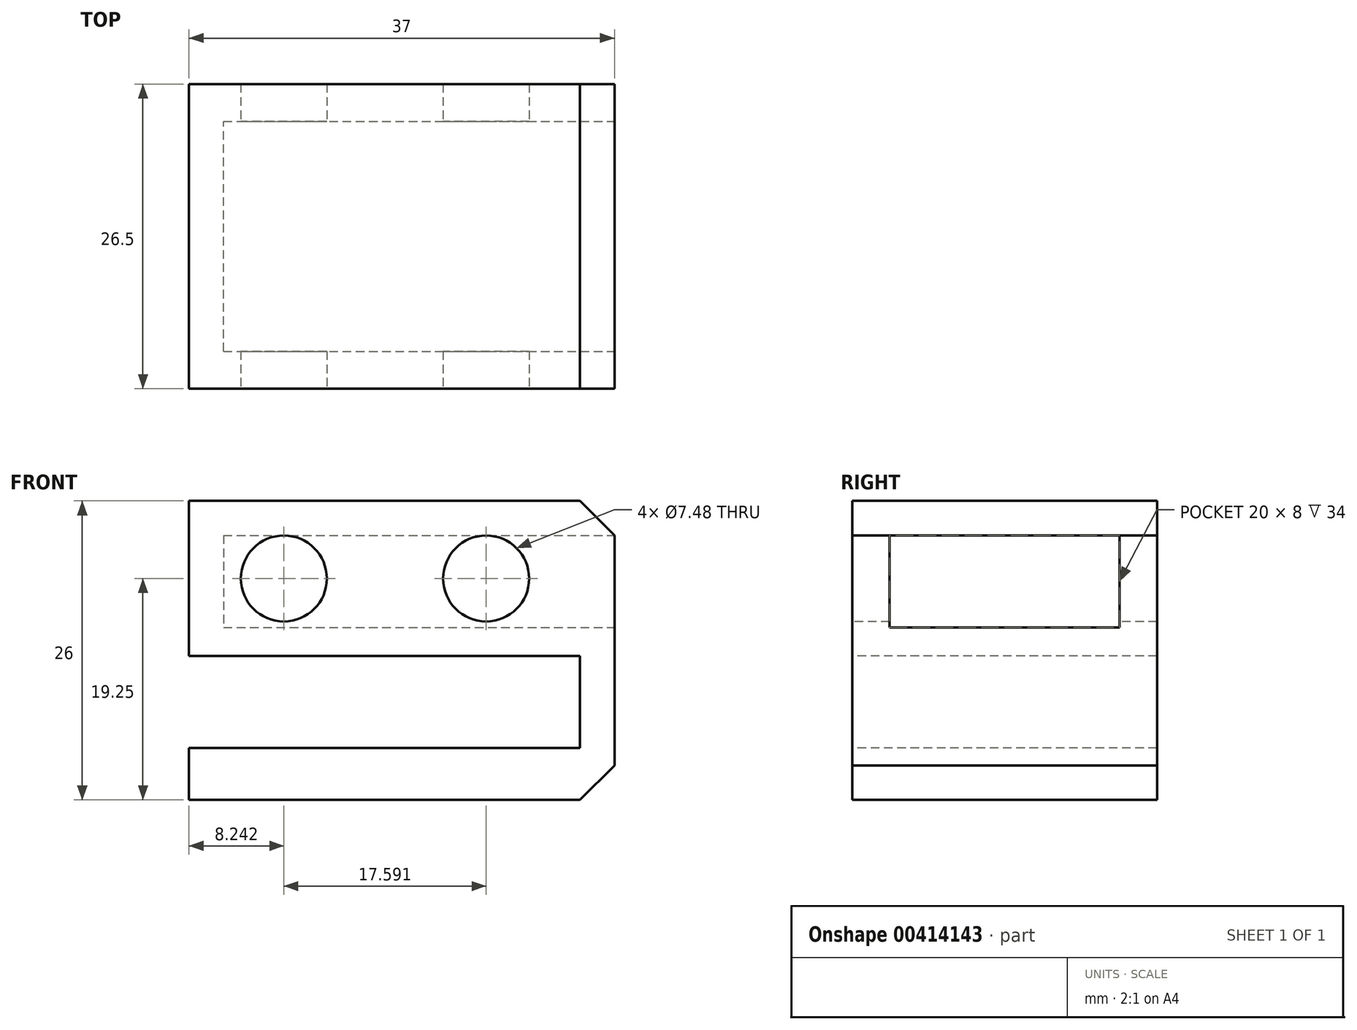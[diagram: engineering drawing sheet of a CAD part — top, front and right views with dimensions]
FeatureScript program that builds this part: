
annotation { "Feature Type Name" : "Feature", "Feature Type Description" : "" }
export const myFeature = defineFeature(function(context is Context, id is Id, definition is map)
    precondition{}
    {
        {
            var Q0;
            Q0=qCreatedBy(makeId("Top.planeOp"),FACE);
            var sketch = newSketch(context, id + "F0", { "sketchPlane" : qUnion([Q0])});
            skLineSegment(sketch, "E0.bottom", {"start": v(-28.8, 0) * mm, "end": v(8.2, 0) * mm});
            skLineSegment(sketch, "E0.top", {"start": v(-28.8, 26.5) * mm, "end": v(8.2, 26.5) * mm});
            skLineSegment(sketch, "E0.left", {"start": v(-28.8, 0) * mm, "end": v(-28.8, 26.5) * mm});
            skLineSegment(sketch, "E0.right", {"start": v(8.2, 0) * mm, "end": v(8.2, 26.5) * mm});
            skSolve(sketch);
        }
        {
            var Q0;
            Q0=makeQuery(id+"F0.imprint","IMPRINT",FACE,{"disambiguationData":[TD([[makeQuery(id+"F0.imprint","IMPRINT",EDGE,{"derivedFrom":sQuery(id+"F0.wireOp",EDGE,"E0.bottom")}),1.0]])]});
            extrude(context, id + "F1", {"entities" : qUnion([Q0]), "oppositeDirection" : true, "depth" : 26 * mm});
        }
        {
            var Q0;
            Q0=qCreatedBy(makeId("Front.planeOp"),FACE);
            var sketch = newSketch(context, id + "F2", { "sketchPlane" : qUnion([Q0])});
            skLineSegment(sketch, "E1.bottom", {"start": v(-28.8, -21.5) * mm, "end": v(5.2, -21.5) * mm});
            skLineSegment(sketch, "E1.top", {"start": v(-28.8, -13.5) * mm, "end": v(5.2, -13.5) * mm});
            skLineSegment(sketch, "E1.left", {"start": v(-28.8, -21.5) * mm, "end": v(-28.8, -13.5) * mm});
            skLineSegment(sketch, "E1.right", {"start": v(5.2, -21.5) * mm, "end": v(5.2, -13.5) * mm});
            skLineSegment(sketch, "E2", {"start": v(-24.14, -21.5) * mm, "end": v(-24.14, -26) * mm, "construction": true});
            skCircle(sketch, "E3", {"center": v(-20.55, -6.75) * mm, "radius": 3.74 * mm});
            skCircle(sketch, "E4", {"center": v(-2.96, -6.75) * mm, "radius": 3.74 * mm});
            skLineSegment(sketch, "E5", {"start": v(-2.96, -6.75) * mm, "end": v(-20.55, -6.75) * mm, "construction": true});
            skLineSegment(sketch, "E6", {"start": v(-11.8, -13.5) * mm, "end": v(-11.8, 0) * mm, "construction": true});
            skPoint(sketch, "E7", {"position": v(-11.8, -6.75) * mm});
            skSolve(sketch);
        }
        {
            var Q0;
            Q0 = qSketchRegion(id + "F2", true);
            extrude(context, id + "F3", {"entities" : qUnion([Q0]), "operationType" : NewBodyOperationType.REMOVE, "endBound" : BoundingType.THROUGH_ALL, "oppositeDirection" : true, "depth" : 25.4 * mm});
        }
        {
            var Q0;
            Q0=makeQuery(id+"F1.opExtrude","SWEPT_FACE",FACE,{"disambiguationData":[OSD([sQuery(id+"F0.wireOp",EDGE,"E0.right")])]});
            var sketch = newSketch(context, id + "F4", { "sketchPlane" : qUnion([Q0])});
            skLineSegment(sketch, "E8.bottom", {"start": v(3.25, -3) * mm, "end": v(23.25, -3) * mm});
            skLineSegment(sketch, "E8.top", {"start": v(3.25, -11) * mm, "end": v(23.25, -11) * mm});
            skLineSegment(sketch, "E8.left", {"start": v(3.25, -3) * mm, "end": v(3.25, -11) * mm});
            skLineSegment(sketch, "E8.right", {"start": v(23.25, -3) * mm, "end": v(23.25, -11) * mm});
            skPoint(sketch, "E9", {"position": v(13.25, -3) * mm});
            skPoint(sketch, "E10", {"position": v(13.25, 0) * mm});
            skLineSegment(sketch, "E11", {"start": v(13.25, 0) * mm, "end": v(13.25, -3) * mm, "construction": true});
            skSolve(sketch);
        }
        {
            var Q0;
            Q0 = qSketchRegion(id + "F4", true);
            extrude(context, id + "F5", {"entities" : qUnion([Q0]), "operationType" : NewBodyOperationType.REMOVE, "oppositeDirection" : true, "depth" : 34 * mm});
        }
        {
            var Q0;
            Q0=makeQuery(id+"F1.opExtrude","SWEPT_FACE",FACE,{"disambiguationData":[OSD([sQuery(id+"F0.wireOp",EDGE,"E0.top")])]});
            var sketch = newSketch(context, id + "F6", { "sketchPlane" : qUnion([Q0])});
            skLineSegment(sketch, "E12", {"start": v(-8.2, -3) * mm, "end": v(-5.2, 0) * mm});
            skLineSegment(sketch, "E13", {"start": v(-5.2, 0) * mm, "end": v(-8.2, 0) * mm});
            skLineSegment(sketch, "E14", {"start": v(-8.2, 0) * mm, "end": v(-8.2, -3) * mm});
            skPoint(sketch, "E15", {"position": v(-8.2, -13) * mm});
            skLineSegment(sketch, "E16", {"start": v(-8.2, -13) * mm, "end": v(-30.48, -13) * mm, "construction": true});
            skLineSegment(sketch, "E17", {"start": v(-30.48, -13) * mm, "end": v(10.14, -13) * mm, "construction": true});
            skLineSegment(sketch, "E18.MirrorCS", {"start": v(-8.2, -26) * mm, "end": v(-8.2, -23) * mm});
            skLineSegment(sketch, "E19.MirrorCS", {"start": v(-5.2, -26) * mm, "end": v(-8.2, -26) * mm});
            skLineSegment(sketch, "E20.MirrorCS", {"start": v(-8.2, -23) * mm, "end": v(-5.2, -26) * mm});
            skSolve(sketch);
        }
        {
            var Q0;
            Q0 = qSketchRegion(id + "F6", true);
            extrude(context, id + "F7", {"entities" : qUnion([Q0]), "operationType" : NewBodyOperationType.REMOVE, "endBound" : BoundingType.THROUGH_ALL, "oppositeDirection" : true, "depth" : 25.4 * mm});
        }
    });
